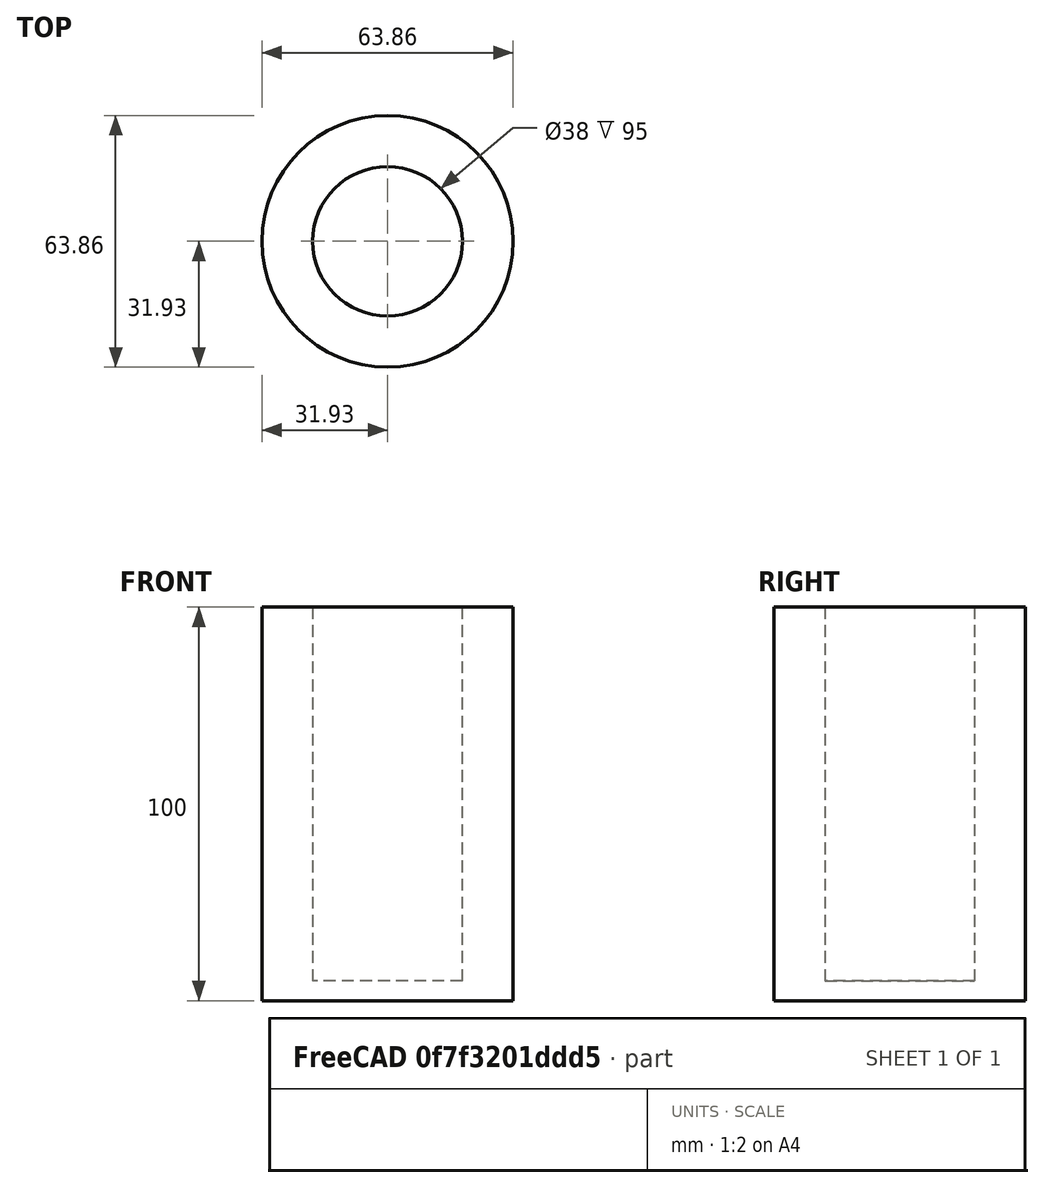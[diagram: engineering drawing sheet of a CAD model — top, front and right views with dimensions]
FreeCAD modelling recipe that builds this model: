
FCSTD DOCUMENT  (FreeCAD 0.19R)
Label: evil cat stick v59
License: All rights reserved
LicenseURL: http://en.wikipedia.org/wiki/All_rights_reserved
objects: Sketcher::SketchObject×2, PartDesign::Pad×2, PartDesign::Body×1
note: 7 computed .brp shape members not serialized (recipe doc carries the construction recipe); baked Part::Feature solids carry a one-line shape summary decoded from their .brp

FEATURE [Sketcher::SketchObject] Sketch
  FullyConstrained = false
  MapMode = 5
  Support = -> [XY_Plane]
  sketch-geometry (1):
    g0: Circle CenterX=0 CenterY=0 CenterZ=0 NormalX=0 NormalY=0 NormalZ=1 AngleXU=0 Radius=31.93
  constraints (1):
    c: Radius(g0) = 31.93
FEATURE [Sketcher::SketchObject] Sketch001
  FullyConstrained = true
  MapMode = 5
  Support = -> [XY_Plane]
  sketch-geometry (2):
    g0: Circle CenterX=0 CenterY=0 CenterZ=0 NormalX=0 NormalY=0 NormalZ=1 AngleXU=0 Radius=19
    g1: Circle CenterX=0 CenterY=0 CenterZ=0 NormalX=0 NormalY=0 NormalZ=1 AngleXU=0 Radius=31.93
  constraints (4):
    c: Coincident(g0,g-1)
    c: Radius(g0) = 19
    c: Coincident(g1,g0)
    c: Radius(g1) = 31.93
FEATURE [PartDesign::Pad] Pad
  Direction = (1,1,1)
  Length = 100
  Length2 = 100
  Profile = -> Sketch001
  Type = 0
FEATURE [PartDesign::Pad] Pad001
  BaseFeature = -> Pad
  Direction = (1,1,1)
  Length = 5
  Length2 = 100
  Profile = -> Sketch
  Type = 0
FEATURE [PartDesign::Body] Body
  Group = -> [Sketch,Sketch001,Pad,Pad001]
  Origin = -> Origin
  Tip = -> Pad001
